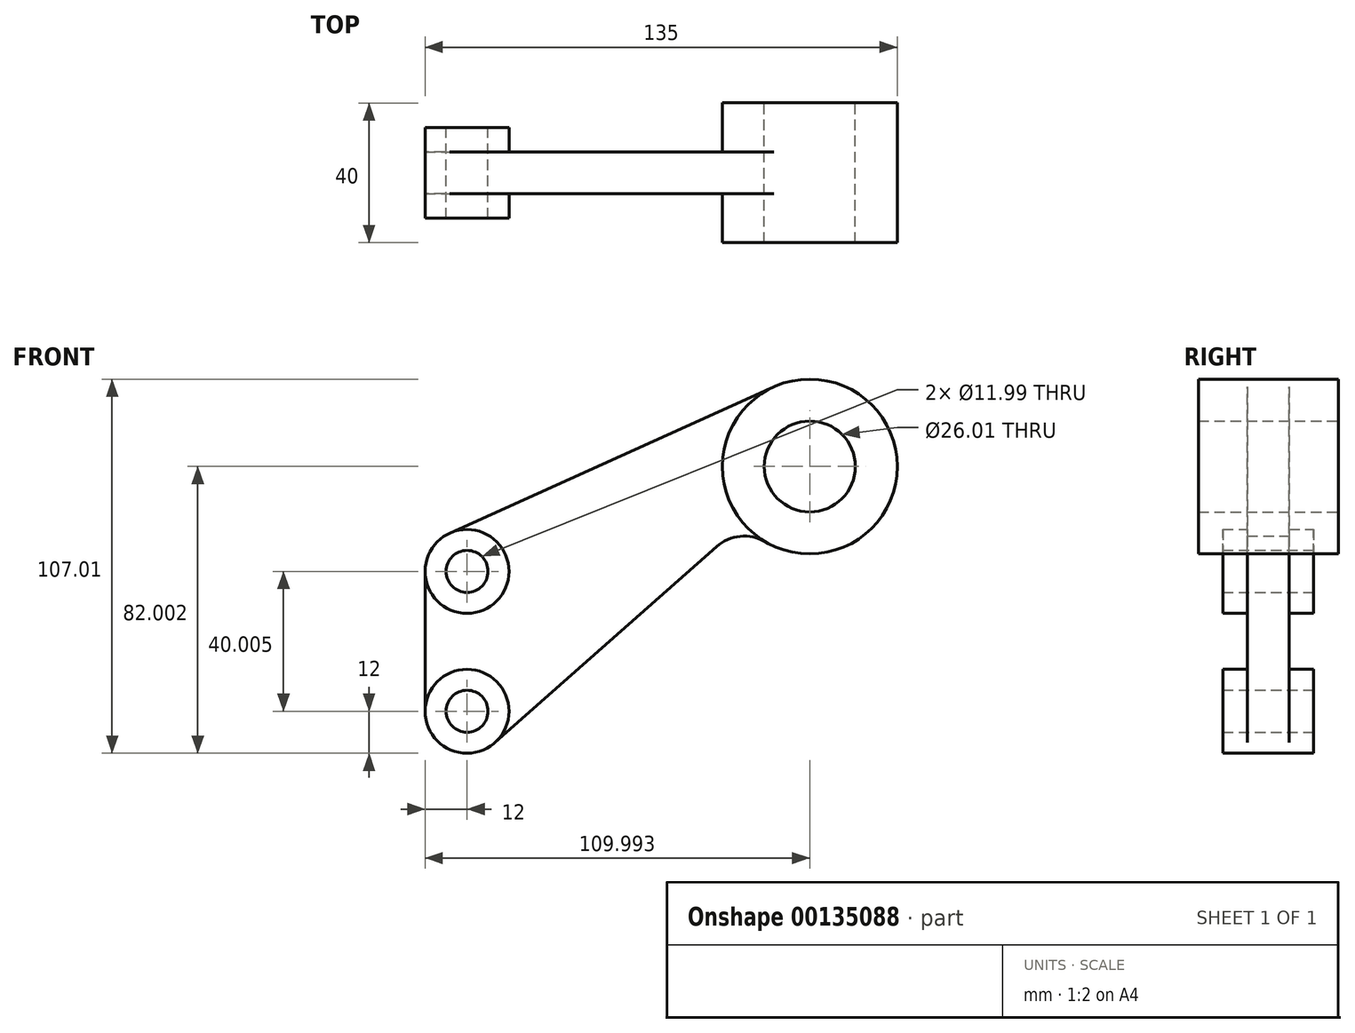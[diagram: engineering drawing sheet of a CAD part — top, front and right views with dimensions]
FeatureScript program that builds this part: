
annotation { "Feature Type Name" : "Feature", "Feature Type Description" : "" }
export const myFeature = defineFeature(function(context is Context, id is Id, definition is map)
    precondition{}
    {
        {
            var Q0;
            Q0=qCreatedBy(makeId("Front.planeOp"),FACE);
            var sketch = newSketch(context, id + "F0", { "sketchPlane" : qUnion([Q0])});
            skPoint(sketch, "E0", {"position": v(0, 0) * mm});
            skPoint(sketch, "E1", {"position": v(0, 40) * mm});
            skCircle(sketch, "E2", {"center": v(0, 0) * mm, "radius": 12 * mm});
            skCircle(sketch, "E3", {"center": v(0, 0) * mm, "radius": 6 * mm});
            skCircle(sketch, "E4", {"center": v(0, 40) * mm, "radius": 12 * mm});
            skCircle(sketch, "E5", {"center": v(0, 40) * mm, "radius": 6 * mm});
            skPoint(sketch, "E6", {"position": v(98, 70) * mm});
            skCircle(sketch, "E7", {"center": v(98, 70) * mm, "radius": 25 * mm});
            skCircle(sketch, "E8", {"center": v(98, 70) * mm, "radius": 13 * mm});
            skLineSegment(sketch, "E9", {"start": v(-4.94, 50.94) * mm, "end": v(87.7, 92.8) * mm});
            skLineSegment(sketch, "E10", {"start": v(-12, 40) * mm, "end": v(-12, 0) * mm});
            skPoint(sketch, "E11", {"position": v(79.26, 38.1) * mm});
            skArc(sketch, "E12", {"start": v(85.33, 48.44) * mm, "mid": v(78.1, 50.03) * mm, "end": v(71.32, 47.08) * mm});
            skLineSegment(sketch, "E13", {"start": v(7.95, -8.99) * mm, "end": v(71.32, 47.08) * mm});
            skSolve(sketch);
        }
        {
            var Q0;
            {var subQ0=sQuery(id+"F0.wireOp",EDGE,"E9");Q0=makeQuery(id+"F0.imprint","IMPRINT",FACE,{"disambiguationData":[TD([[makeQuery(id+"F0.imprint","IMPRINT",EDGE,{"derivedFrom":subQ0}),-1.0]])]});}
            extrude(context, id + "F1", {"entities" : qUnion([Q0]), "depth" : 6 * mm});
        }
        {
            var Q0;
            Q0=makeQuery(id+"F0.imprint","IMPRINT",FACE,{"disambiguationData":[TD([[makeQuery(id+"F0.imprint","IMPRINT",EDGE,{"derivedFrom":sQuery(id+"F0.wireOp",EDGE,"E5")}),-1.0]])]});
            var Q1;
            Q1=makeQuery(id+"F0.imprint","IMPRINT",FACE,{"disambiguationData":[TD([[makeQuery(id+"F0.imprint","IMPRINT",EDGE,{"derivedFrom":sQuery(id+"F0.wireOp",EDGE,"E3")}),-1.0]])]});
            extrude(context, id + "F2", {"entities" : qUnion([Q0, Q1]), "operationType" : NewBodyOperationType.ADD, "depth" : 13 * mm});
        }
        {
            var Q0;
            Q0=makeQuery(id+"F0.imprint","IMPRINT",FACE,{"disambiguationData":[TD([[makeQuery(id+"F0.imprint","IMPRINT",EDGE,{"derivedFrom":sQuery(id+"F0.wireOp",EDGE,"E8")}),-1.0]])]});
            extrude(context, id + "F3", {"entities" : qUnion([Q0]), "operationType" : NewBodyOperationType.ADD, "depth" : 20 * mm});
        }
        {
            var Q0;
            Q0=makeQuery(id+"F1.opExtrude","SWEPT_BODY",BODY,{"disambiguationData":[OSD([sQuery(id+"F0.wireOp",EDGE,"E2"),sQuery(id+"F0.wireOp",EDGE,"E4"),sQuery(id+"F0.wireOp",EDGE,"E7"),sQuery(id+"F0.wireOp",EDGE,"E9"),sQuery(id+"F0.wireOp",EDGE,"E10"),sQuery(id+"F0.wireOp",EDGE,"E12"),sQuery(id+"F0.wireOp",EDGE,"E13")])]});
            var Q1;
            Q1=qCreatedBy(makeId("Front.planeOp"),FACE);
            mirror(context, id + "F4", {"operationType" : NewBodyOperationType.ADD, "entities" : qUnion([Q0]), "mirrorPlane" : qUnion([Q1])});
        }
    });
